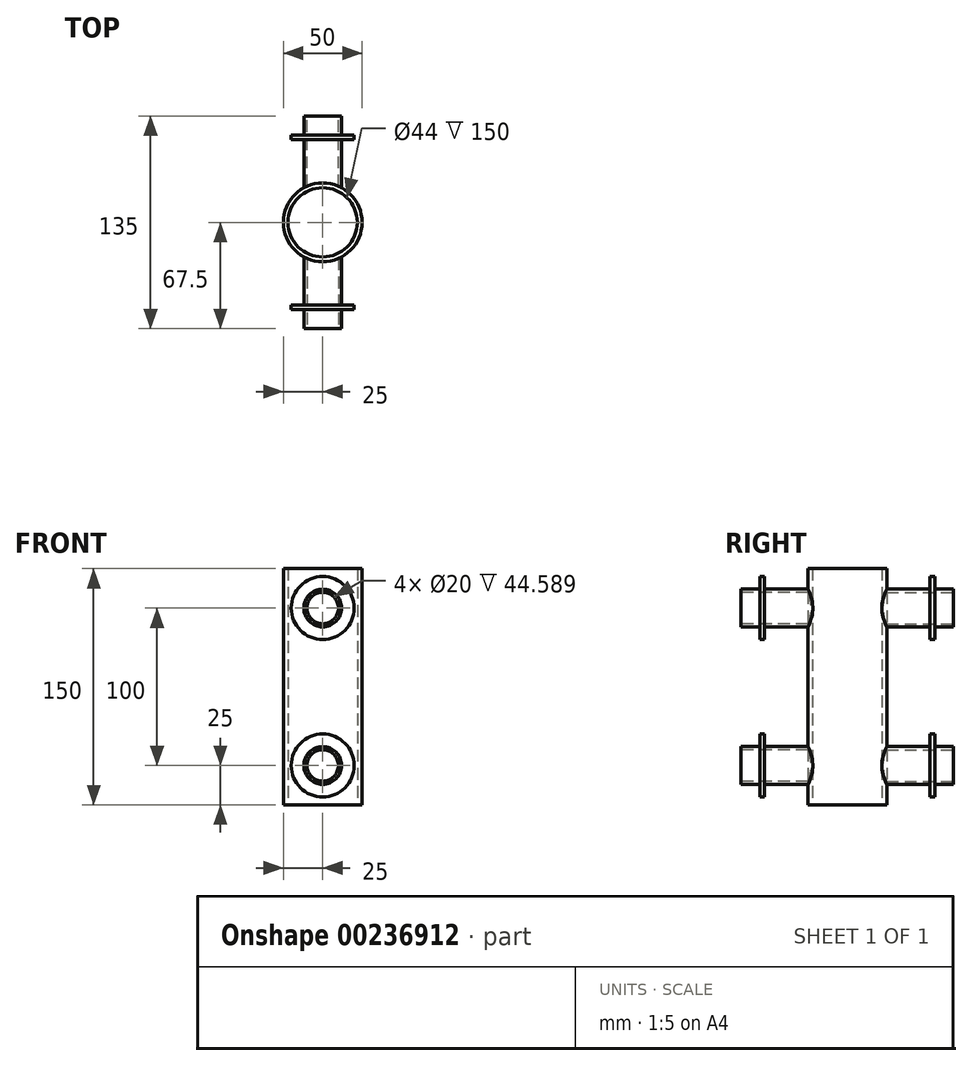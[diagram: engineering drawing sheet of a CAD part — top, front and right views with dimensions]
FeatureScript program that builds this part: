
annotation { "Feature Type Name" : "Feature", "Feature Type Description" : "" }
export const myFeature = defineFeature(function(context is Context, id is Id, definition is map)
    precondition{}
    {
        {
            var Q0;
            Q0=qCreatedBy(makeId("Front.planeOp"),FACE);
            cPlane(context, id + "F0", {"entities" : qUnion([Q0]), "cplaneType" : CPlaneType.OFFSET, "offset" : 135 * mm, "width" : 150 * mm, "height" : 150 * mm});
        }
        {
            var Q0;
            Q0=qCreatedBy(makeId("Front.planeOp"),FACE);
            cPlane(context, id + "F1", {"entities" : qUnion([Q0]), "cplaneType" : CPlaneType.OFFSET, "offset" : 67.5 * mm, "width" : 150 * mm, "height" : 150 * mm});
        }
        {
            var Q0;
            Q0=qCreatedBy(id+"F1.planeOp",FACE);
            var sketch = newSketch(context, id + "F2", { "sketchPlane" : qUnion([Q0])});
            skLineSegment(sketch, "E0", {"start": v(0, 25) * mm, "end": v(0, 0) * mm, "construction": true});
            skLineSegment(sketch, "E1", {"start": v(0, 0) * mm, "end": v(0, -99.27) * mm, "construction": true});
            skLineSegment(sketch, "E2", {"start": v(0, 25) * mm, "end": v(0, 125) * mm, "construction": true});
            skLineSegment(sketch, "E3", {"start": v(0, 125) * mm, "end": v(0, 150) * mm, "construction": true});
            skSolve(sketch);
        }
        {
            var Q0;
            Q0=qCreatedBy(makeId("Top.planeOp"),FACE);
            var sketch = newSketch(context, id + "F3", { "sketchPlane" : qUnion([Q0])});
            skLineSegment(sketch, "E4", {"start": v(0, 6.88) * mm, "end": v(0, -67.5) * mm, "construction": true});
            skLineSegment(sketch, "E5", {"start": v(0, -67.5) * mm, "end": v(0, -98.54) * mm, "construction": true});
            skSolve(sketch);
        }
        {
            var Q0;
            Q0=qCreatedBy(makeId("Top.planeOp"),FACE);
            var sketch = newSketch(context, id + "F4", { "sketchPlane" : qUnion([Q0])});
            skCircle(sketch, "E6", {"center": v(0, -67.5) * mm, "radius": 22 * mm});
            skCircle(sketch, "E7", {"center": v(0, -67.5) * mm, "radius": 25 * mm});
            skSolve(sketch);
        }
        {
            var Q0;
            Q0=qCreatedBy(id+"F0.planeOp",FACE);
            var sketch = newSketch(context, id + "F5", { "sketchPlane" : qUnion([Q0])});
            skCircle(sketch, "E8", {"center": v(0, 25) * mm, "radius": 10 * mm});
            skCircle(sketch, "E9", {"center": v(0, 25) * mm, "radius": 12 * mm});
            skCircle(sketch, "E10", {"center": v(0, 125) * mm, "radius": 10 * mm});
            skCircle(sketch, "E11", {"center": v(0, 125) * mm, "radius": 12 * mm});
            skCircle(sketch, "E12", {"center": v(0, 25) * mm, "radius": 20 * mm});
            skCircle(sketch, "E13", {"center": v(0, 125) * mm, "radius": 20 * mm});
            skSolve(sketch);
        }
        {
            var Q0;
            Q0=makeQuery(id+"F4.imprint","IMPRINT",FACE,{"disambiguationData":[TD([[makeQuery(id+"F4.imprint","IMPRINT",EDGE,{"derivedFrom":sQuery(id+"F4.wireOp",EDGE,"E6")}),-1.0]])]});
            var Q1;
            Q1=sQuery(id+"F2.wireOp",VERTEX,"E3.end");
            extrude(context, id + "F6", {"entities" : qUnion([Q0]), "endBound" : BoundingType.UP_TO_VERTEX, "endBoundEntityVertex" : qUnion([Q1]), "depth" : 25 * mm});
        }
        {
            var Q0;
            Q0=makeQuery(id+"F5.imprint","IMPRINT",FACE,{"disambiguationData":[TD([[makeQuery(id+"F5.imprint","IMPRINT",EDGE,{"derivedFrom":sQuery(id+"F5.wireOp",EDGE,"E10")}),-1.0]])]});
            var Q1;
            Q1=makeQuery(id+"F5.imprint","IMPRINT",FACE,{"disambiguationData":[TD([[makeQuery(id+"F5.imprint","IMPRINT",EDGE,{"derivedFrom":sQuery(id+"F5.wireOp",EDGE,"E8")}),-1.0]])]});
            var Q2;
            Q2=makeQuery(id+"F6.opExtrude","SWEPT_BODY",BODY,{"disambiguationData":[OSD([sQuery(id+"F4.wireOp",EDGE,"E6"),sQuery(id+"F4.wireOp",EDGE,"E7")])]});
            extrude(context, id + "F7", {"entities" : qUnion([Q0, Q1]), "endBound" : BoundingType.UP_TO_BODY, "oppositeDirection" : true, "endBoundEntityBody" : qUnion([Q2]), "depth" : 25 * mm});
        }
        {
            var Q0;
            Q0=makeQuery(id+"F5.imprint","IMPRINT",FACE,{"disambiguationData":[TD([[makeQuery(id+"F5.imprint","IMPRINT",EDGE,{"derivedFrom":sQuery(id+"F5.wireOp",EDGE,"E11")}),-1.0]])]});
            var Q1;
            Q1=makeQuery(id+"F5.imprint","IMPRINT",FACE,{"disambiguationData":[TD([[makeQuery(id+"F5.imprint","IMPRINT",EDGE,{"derivedFrom":sQuery(id+"F5.wireOp",EDGE,"E9")}),-1.0]])]});
            extrude(context, id + "F8", {"entities" : qUnion([Q0, Q1]), "oppositeDirection" : true, "depth" : 15 * mm, "hasSecondDirection" : true, "secondDirectionOppositeDirection" : true, "secondDirectionDepth" : 12 * mm});
        }
        {
            var Q0;
            Q0=makeQuery(id+"F7.opExtrude","SWEPT_BODY",BODY,{"disambiguationData":[OSD([sQuery(id+"F5.wireOp",EDGE,"E10"),sQuery(id+"F5.wireOp",EDGE,"E11")])]});
            var Q1;
            Q1=makeQuery(id+"F8.opExtrude","SWEPT_BODY",BODY,{"disambiguationData":[OSD([sQuery(id+"F5.wireOp",EDGE,"E11"),sQuery(id+"F5.wireOp",EDGE,"E13")])]});
            var Q2;
            Q2=makeQuery(id+"F7.opExtrude","SWEPT_BODY",BODY,{"disambiguationData":[OSD([sQuery(id+"F5.wireOp",EDGE,"E8"),sQuery(id+"F5.wireOp",EDGE,"E9")])]});
            var Q3;
            Q3=makeQuery(id+"F8.opExtrude","SWEPT_BODY",BODY,{"disambiguationData":[OSD([sQuery(id+"F5.wireOp",EDGE,"E9"),sQuery(id+"F5.wireOp",EDGE,"E12")])]});
            var Q4;
            Q4=qCreatedBy(id+"F1.planeOp",FACE);
            mirror(context, id + "F9", {"operationType" : NewBodyOperationType.ADD, "entities" : qUnion([Q0, Q1, Q2, Q3]), "mirrorPlane" : qUnion([Q4])});
        }
    });
